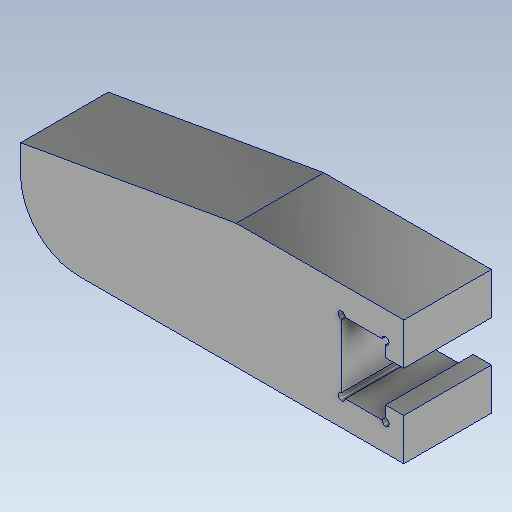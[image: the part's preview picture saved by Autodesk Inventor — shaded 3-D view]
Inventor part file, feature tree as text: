
AUTODESK INVENTOR PART (.ipt)
format: ipt  version: 2025.2 (Build 292293000, 293)  size: 322,048 bytes
history: native  units: mm
features: extrude x2, sketch x2, fillet x1
ambient origin geometry x8: Origin, YZ Plane, XZ Plane, XY Plane, X Axis, Y Axis, Z Axis, Center Point
bodies: Solid2 (feature_tree)
feature tree (5):
  extrude  "Extrusion2"  Depth=44.0mm
  extrude  "Extrusion7"  Depth=12.0mm TaperAngle=0.0deg
  fillet  "Rundung4"  Radius=15.6mm
  sketch  "Sketch5"  dims[d41=6.0mm d48=44.0mm]
  sketch  "Sketch11"  dims[d50=2.5mm d56=12.0mm d57=0.0mm d67=15.6mm d87=5.6mm d88=9.65mm d99=1.0mm d100=1.0mm d101=1.0mm d102=1.0mm d103=0.0mm d104=0.0mm d111=8.0mm d115=1.745329mm d116=30.0mm d117=0.0mm]
